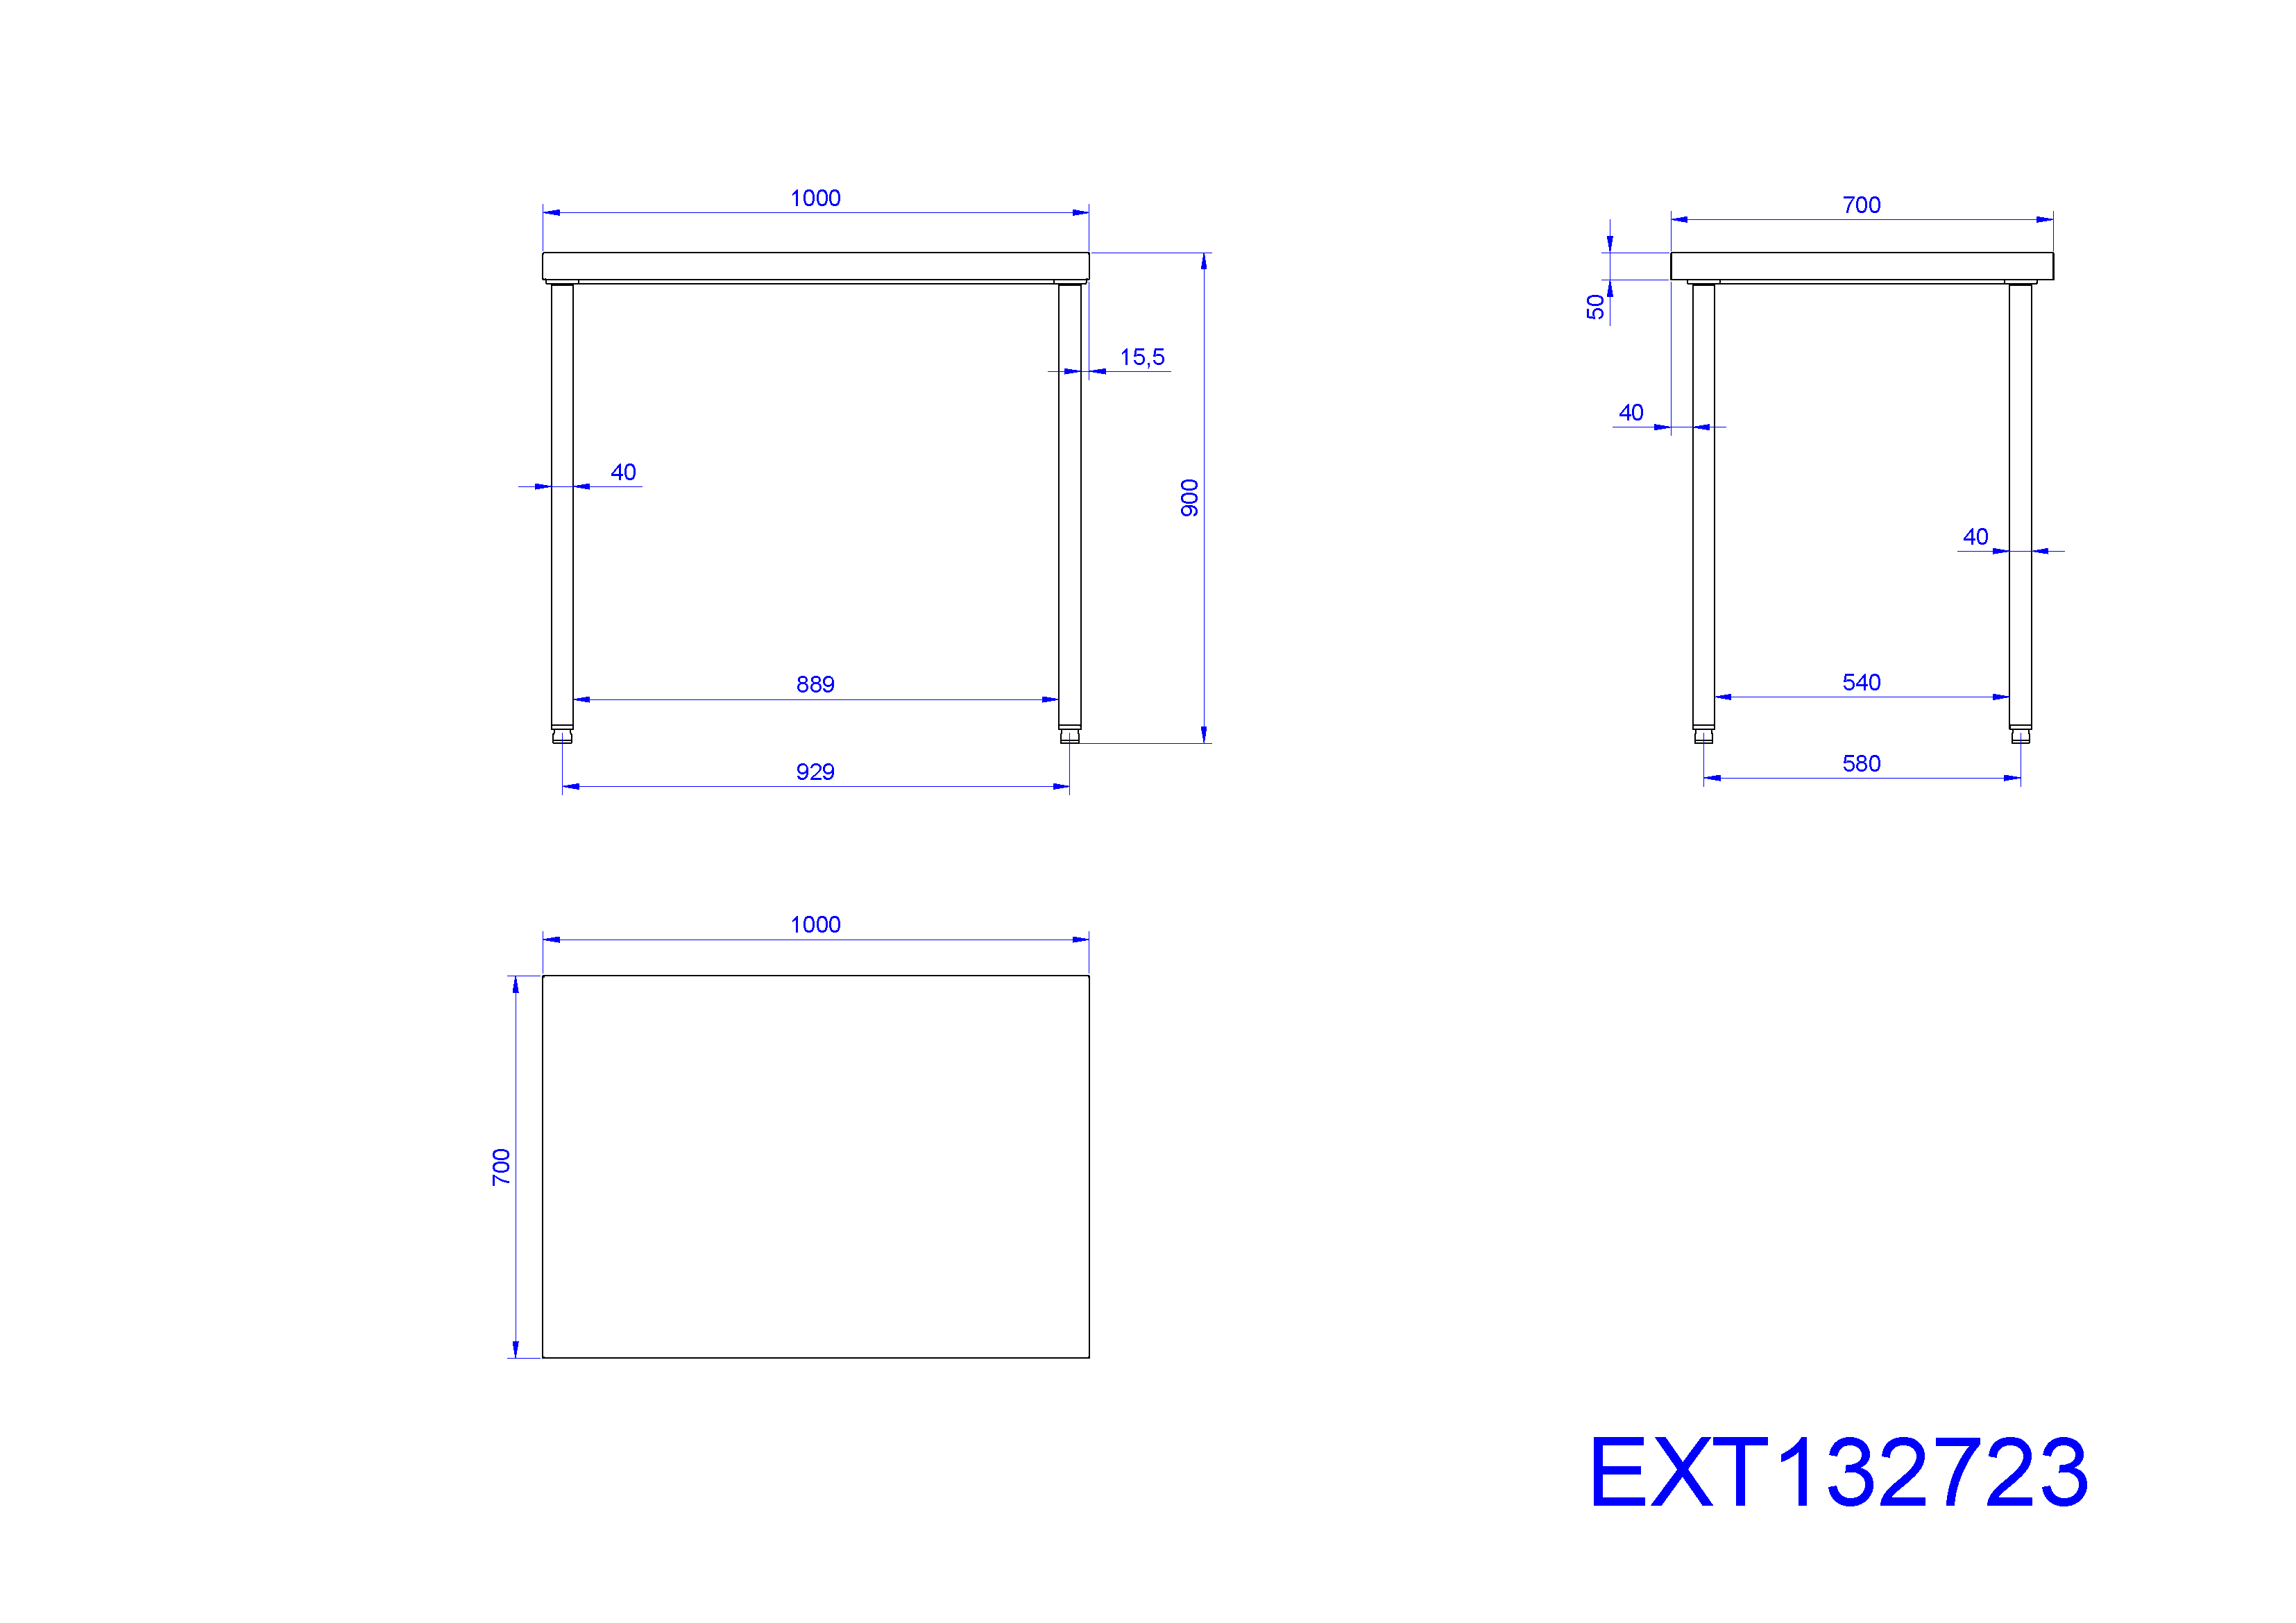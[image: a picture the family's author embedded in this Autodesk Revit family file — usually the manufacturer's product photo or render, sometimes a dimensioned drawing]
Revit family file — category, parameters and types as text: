
# Revit family: QF_ELECTROLUXPROFESSIONAL_133050_TG1400EN
name_source: partatom
category: Specialty Equipment
units: mm (PartAtom-declared; Revit-internal decimal feet)

## family parameters
Always vertical = Yes
Cut with Voids When Loaded = No
Part Type = Normal
Room Calculation Point = No
Round Connector Dimension = Use Diameter
Shared = No
Work Plane-Based = No

## types (1)
- Standard
    Accessory = No
    Cold Water Size = 0 mm
    Compressed Air Pressure = 0.0 Pa
    Compressed Air Size = 0 mm
    Compressed Air Volume = 0.0 L/s
    Condensate Return Size = 0 mm
    Cycle = 0 Hz
    Default Elevation = 0 mm  [stored 0 ft]
    Depth Actual = 700 mm  [stored 2.29659 ft]
    Description = WORK TABLE 1400 MM
    Direct Waste Size = 0 mm
    Gas Input Pressure = 0
    Gas KW = 0
    Gas Size = 0 mm
    HP = 0 HP
    Height Actual = 900 mm  [stored 2.95276 ft]
    Hot Water Size = 0 mm
    Item Number = 133050
    Length Actual = 1400 mm  [stored 4.59318 ft]
    Manufacturer = Electrolux Professional
    Model = TG1400EN
    Phase = 0
    Refrigerant Compressor Remote = Yes
    Refrigeration Liquid Line Size = 0 mm  [stored 0 ft]
    Refrigeration Suction Line Size = 0 mm  [stored 0 ft]
    Steam Consumption per Hour = 0
    Steam Supply Maximum Pressure = 0.0 Pa
    Steam Supply Minimum Pressure = 0.0 Pa
    Steam Supply Size = 0 mm
    URL = http://www.electroluxprofessional.com
    URL Manufacturer = http://www.electroluxprofessional.com
    Volts = 0 V
    Watts = 0 W
    Weight = 45.00 kg

note: source unit labels omitted for Gas Input Pressure — the stored unit's dimension contradicts the parameter name (converter mislabeling)

note: [stored X ft] marks values corroborated as IEEE doubles in the binary element streams (Revit-internal decimal feet)

## geometry (parser evidence)
native form markers: Sweep x3
no freeform markers — native parametric forms only
